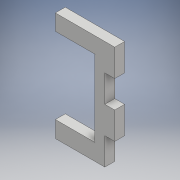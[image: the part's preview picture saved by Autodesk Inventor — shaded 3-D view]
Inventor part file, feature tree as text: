
AUTODESK INVENTOR PART (.ipt)
format: ipt  version: 2018 (Build 220112000, 112)  size: 130,560 bytes
history: native  units: mm
features: extrude x3, sketch x3, other x1
ambient origin geometry x8: Origin, YZ Plane, XZ Plane, XY Plane, X Axis, Y Axis, Z Axis, Center Point
bodies: Body1 (feature_tree)
feature tree (7):
  other  "Sólido1"
  extrude  "Extrusión1"  Depth=3.0mm
  extrude  "Extrusión2"  Depth=3.0mm TaperAngle=0.0deg
  extrude  "Extrusión4"  Depth=3.0mm
  sketch  "Boceto1"  dims[d0=8.25mm d1=3.0mm]
  sketch  "Boceto2"  dims[d3=8.25mm d11=3.0mm d12=0.0mm]
  sketch  "Boceto5"  dims[d16=10.0mm d17=0.0mm d22=0.168mm d23=3.0mm d24=0.0mm]
